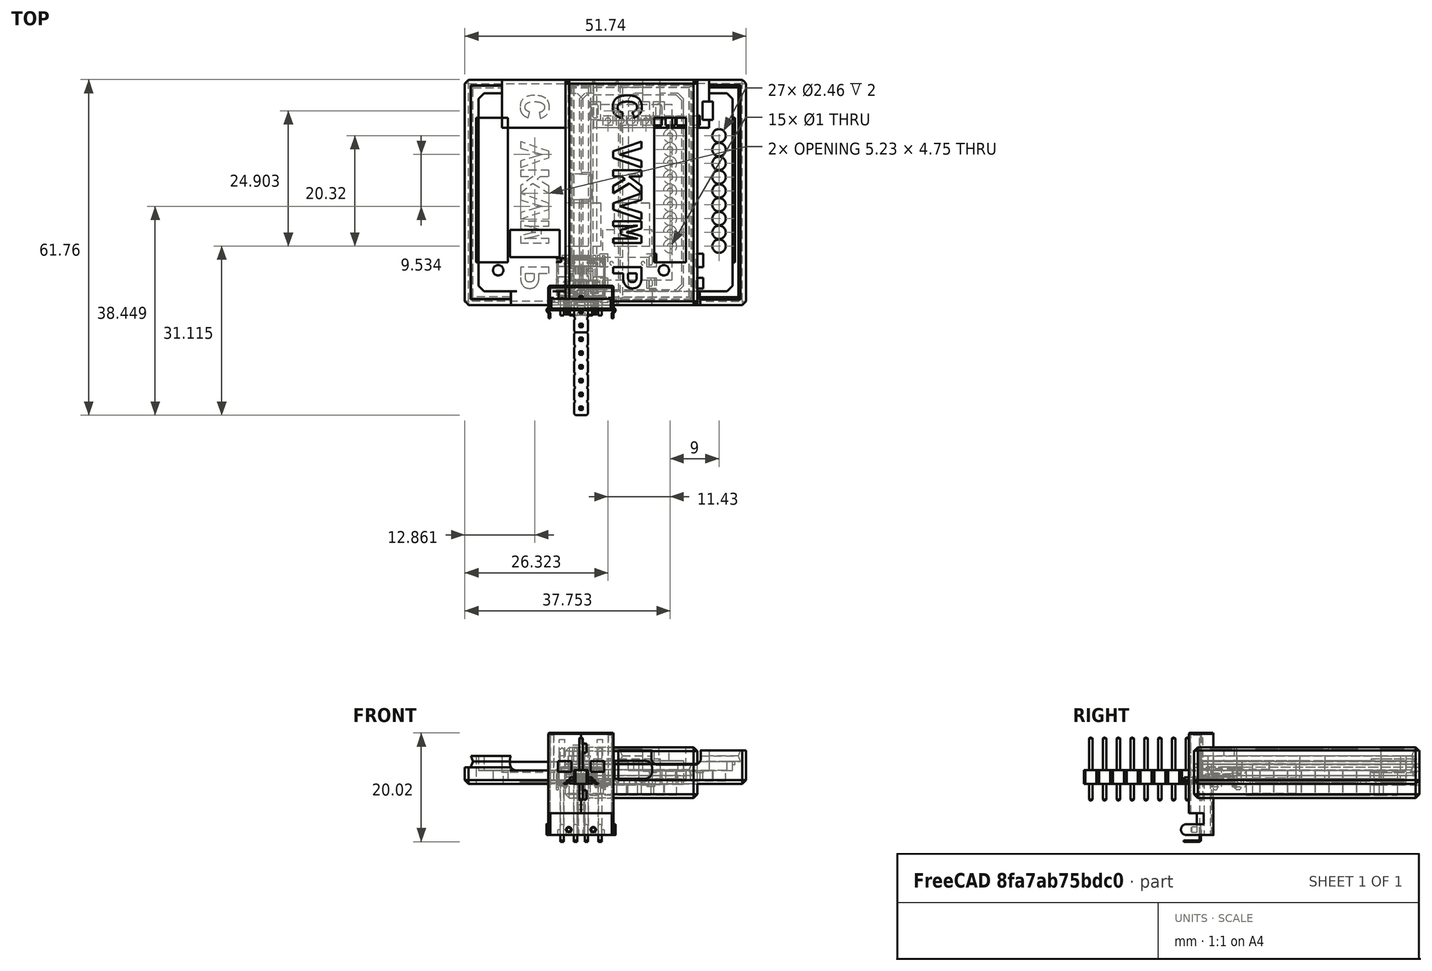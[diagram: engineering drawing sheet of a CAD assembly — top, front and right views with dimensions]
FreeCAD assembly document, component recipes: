
FREECAD ASSEMBLY — COMPONENT RECIPES ("case")

This assembly document has 10 components, labeled P0..P9 below (a component is one placed body or linked part). 4 of them carry a construction recipe — the FreeCAD feature program that regenerates the part from scratch, quoted from this document or its linked companion documents; the rest are supplied as boundary geometry only. No exploded tour is included for this assembly.
COMPONENT P0 — recipe-attached ("CaseAllPinsClone", modeled in this document).
Construction recipe (the document's own serialized feature program — sketch geometry with constraints, then the solid features built on it; lengths are millimeters unless a unit is written):

FEATURE [Sketcher::SketchObject] Sketch  label="OuterSketch"
  AttachmentOffset = pos=(0,0,-2.56) rot=(0,0,1;0rad)
  FullyConstrained = true
  MapMode = 5
  Placement = pos=(0,0,-2.56) rot=(0,0,1;0rad)
  Support = -> [XY_Plane031]
  expr: .AttachmentOffset.Base.z = -(<<Param>>.T_WALL + <<Param>>.T_Z)
  expr: .Constraints.X1 = -(<<Param>>.T_WALL + <<Param>>.S_SIDE + <<Param>>.T_XY)
  expr: .Constraints.X2 = 730 mil + <<Param>>.T_WALL + <<Param>>.S_SIDE + <<Param>>.T_XY
  expr: .Constraints.Y1 = 60 mil - <<Param>>.T_WALL - <<Param>>.S_SIDE - <<Param>>.T_XY
  expr: .Constraints.Y2 = 1470 mil + <<Param>>.T_WALL + <<Param>>.S_SIDE + <<Param>>.T_XY
  sketch-geometry (4):
    g0: LineSegment StartX=-2.83 StartY=-1.306 StartZ=0 EndX=21.372 EndY=-1.306 EndZ=0
    g1: LineSegment StartX=21.372 StartY=-1.306 StartZ=0 EndX=21.372 EndY=40.168 EndZ=0
    g2: LineSegment StartX=21.372 StartY=40.168 StartZ=0 EndX=-2.83 EndY=40.168 EndZ=0
    g3: LineSegment StartX=-2.83 StartY=40.168 StartZ=0 EndX=-2.83 EndY=-1.306 EndZ=0
  constraints (12):
    c: Coincident(g0,g1)
    c: Coincident(g1,g2)
    c: Coincident(g2,g3)
    c: Coincident(g3,g0)
    c: Horizontal(g0)
    c: Horizontal(g2)
    c: Vertical(g1)
    c: Vertical(g3)
    c: DistanceX(g0) = -2.83  'X1'
    c: DistanceY(g0) = -1.306  'Y1'
    c: DistanceX(g1) = 21.372  'X2'
    c: DistanceY(g1) = 40.168  'Y2'
FEATURE [PartDesign::Pad] Pad  label="OuterPad"
  Direction = (0,0,1)
  Length = 9.33
  Length2 = 10
  Profile = -> Sketch
  ReferenceAxis = -> Sketch [N_Axis]
  Type = 0
  expr: Length = <<Param>>.T_BOARD + 3.21 mm + 2 * (<<Param>>.T_WALL + <<Param>>.T_Z)
FEATURE [Sketcher::SketchObject] Sketch001  label="BoardSketch"
  AttachmentOffset = pos=(0,0,-0.06) rot=(0,0,1;0rad)
  FullyConstrained = true
  MapMode = 5
  Placement = pos=(0,0,-0.06) rot=(0,0,1;0rad)
  Support = -> [XY_Plane031]
  expr: .AttachmentOffset.Base.z = -<<Param>>.T_Z
  expr: Constraints[22] = <<OuterSketch>>.Constraints.Y1 + <<Param>>.T_WALL
  expr: Constraints[23] = <<OuterSketch>>.Constraints.X1 + <<Param>>.T_WALL
  expr: Constraints[24] = <<OuterSketch>>.Constraints.X2 - <<Param>>.T_WALL
  expr: Constraints[25] = <<OuterSketch>>.Constraints.Y2 - <<Param>>.T_WALL
  expr: Constraints[35] = max(0 mm; 0.76 mm - <<Param>>.S_SIDE - <<Param>>.T_XY)
  expr: Constraints[36] = 50 mil + <<Param>>.S_SIDE + <<Param>>.T_XY - min(0 mm; 0.76 mm - <<Param>>.S_SIDE - <<Param>>.T_XY)
  expr: Constraints[37] = 560 mil + 2 * (<<Param>>.S_SIDE + <<Param>>.T_XY)
  expr: Constraints[38] = 210 mil - 2 * (<<Param>>.S_SIDE + <<Param>>.T_XY)
  expr: Constraints[39] = 40 mil
  sketch-geometry (14):
    g0: LineSegment StartX=-0.33 StartY=2.21 StartZ=0 EndX=0.686 EndY=1.194 EndZ=0
    g1: LineSegment StartX=0.686 StartY=1.194 StartZ=0 EndX=17.856 EndY=1.194 EndZ=0
    g2: LineSegment StartX=17.856 StartY=1.194 StartZ=0 EndX=18.872 EndY=2.21 EndZ=0
    g3: LineSegment StartX=18.872 StartY=2.21 StartZ=0 EndX=18.872 EndY=36.652 EndZ=0
    g4: LineSegment StartX=18.872 StartY=36.652 StartZ=0 EndX=17.856 EndY=37.668 EndZ=0
    g5: LineSegment StartX=17.856 StartY=37.668 StartZ=0 EndX=0.686 EndY=37.668 EndZ=0
    g6: LineSegment StartX=0.686 StartY=37.668 StartZ=0 EndX=-0.33 EndY=36.652 EndZ=0
    g7: LineSegment StartX=-0.33 StartY=36.652 StartZ=0 EndX=-0.33 EndY=22.784 EndZ=0
    g8: LineSegment StartX=-0.33 StartY=22.784 StartZ=0 EndX=1.27 EndY=22.784 EndZ=0
    g9: LineSegment StartX=1.7 StartY=22.354 StartZ=0 EndX=1.7 EndY=18.54 EndZ=0
    g10: LineSegment StartX=1.27 StartY=18.11 StartZ=0 EndX=-0.33 EndY=18.11 EndZ=0
    g11: LineSegment StartX=-0.33 StartY=18.11 StartZ=0 EndX=-0.33 EndY=2.21 EndZ=0
    g12: ArcOfCircle CenterX=1.27 CenterY=22.354 CenterZ=0 NormalX=0 NormalY=0 NormalZ=1 AngleXU=0 Radius=0.43 StartAngle=-2.7e-15 EndAngle=1.5708
    g13: ArcOfCircle CenterX=1.27 CenterY=18.54 CenterZ=0 NormalX=0 NormalY=0 NormalZ=1 AngleXU=0 Radius=0.43 StartAngle=4.71239 EndAngle=6.28319
  constraints (40):
    c: Coincident(g0,g1)
    c: Horizontal(g1)
    c: Coincident(g1,g2)
    c: Coincident(g2,g3)
    c: Vertical(g3)
    c: Coincident(g3,g4)
    c: Coincident(g4,g5)
    c: Horizontal(g5)
    c: Coincident(g5,g6)
    c: Coincident(g6,g7)
    c: Vertical(g7)
    c: Coincident(g7,g8)
    c: Vertical(g9)
    c: Horizontal(g10)
    c: Coincident(g10,g11)
    c: Coincident(g11,g0)
    c: Vertical(g11)
    c: Horizontal(g0,g2)
    c: Vertical(g10,g7)
    c: Horizontal(g6,g3)
    c: Vertical(g5,g0)
    c: Vertical(g1,g4)
    c: DistanceY(g0) = 1.194
    c: DistanceX(g0) = -0.33
    c: DistanceX(g3) = 18.872
    c: DistanceY(g4) = 37.668
    c: Equal(g6,g4)
    c: Equal(g4,g2)
    c: Angle(g4,g3) = 2.35619
    c: Horizontal(g8)
    c: Tangent(g8,g12) = 1.5708
    c: Tangent(g9,g12) = 1.5708
    c: Tangent(g9,g13) = 1.5708
    c: Tangent(g10,g13) = 1.5708
    c: Equal(g13,g12)
    c: Radius(g12) = 0.43
    c: DistanceX(g8,g8) = 1.6
    c: DistanceY(g8,g5) = 14.884
    c: DistanceY(g10,g7) = 4.674
    c: DistanceX(g4,g4) = 1.016
FEATURE [Sketcher::SketchObject] Sketch002  label="LedSketch"
  FullyConstrained = true
  MapMode = 5
  Support = -> [XY_Plane031]
  expr: Constraints[0] = <<Param>>.D_LED + 2 * <<Param>>.T_XY
  expr: Constraints[1] = 600 mil
  expr: Constraints[2] = 200 mil
  sketch-geometry (1):
    g0: Circle CenterX=15.24 CenterY=5.08 CenterZ=0 NormalX=0 NormalY=0 NormalZ=1 AngleXU=0 Radius=0.955
  constraints (3):
    c: Diameter(g0) = 1.91
    c: DistanceX(g0) = 15.24
    c: DistanceY(g0) = 5.08
FEATURE [Sketcher::SketchObject] Sketch003  label="UsbCSketch"
  AttachmentOffset = pos=(0,0,-7.427) rot=(0,0,1;0rad)
  FullyConstrained = true
  MapMode = 5
  Placement = pos=(0,7.427,1.6e-15) rot=(1,0,0;1.5708rad)
  Support = -> [XZ_Plane031]
  expr: .AttachmentOffset.Base.z = -(5 mil + 7.3 mm)
  expr: .Constraints.D1 = 3.16 mm + 2 * <<Param>>.T_Z
  expr: .Constraints.R1 = 1.1 mm + <<Param>>.T_XY + <<Param>>.T_Z
  expr: .Constraints.W1 = 8.95 mm + 2 * <<Param>>.T_XY
  expr: .Constraints.X1 = 335 mil
  expr: .Constraints.Z1 = <<Param>>.T_BOARD + 0.05 mm - <<Param>>.T_Z
  sketch-geometry (9):
    g0: LineSegment StartX=5.194 StartY=4.27 StartZ=0 EndX=11.824 EndY=4.27 EndZ=0
    g1: LineSegment StartX=13.064 StartY=3.03 StartZ=0 EndX=13.064 EndY=2.23 EndZ=0
    g2: LineSegment StartX=11.824 StartY=0.99 StartZ=0 EndX=5.194 EndY=0.99 EndZ=0
    g3: LineSegment StartX=3.954 StartY=2.23 StartZ=0 EndX=3.954 EndY=3.03 EndZ=0
    g4: ArcOfCircle CenterX=5.194 CenterY=3.03 CenterZ=0 NormalX=0 NormalY=0 NormalZ=1 AngleXU=0 Radius=1.24 StartAngle=1.5708 EndAngle=3.14159
    g5: ArcOfCircle CenterX=5.194 CenterY=2.23 CenterZ=0 NormalX=0 NormalY=0 NormalZ=1 AngleXU=0 Radius=1.24 StartAngle=3.14159 EndAngle=4.71239
    g6: ArcOfCircle CenterX=11.824 CenterY=2.23 CenterZ=0 NormalX=0 NormalY=0 NormalZ=1 AngleXU=0 Radius=1.24 StartAngle=4.71239 EndAngle=6.28319
    g7: ArcOfCircle CenterX=11.824 CenterY=3.03 CenterZ=0 NormalX=0 NormalY=0 NormalZ=1 AngleXU=0 Radius=1.24 StartAngle=0 EndAngle=1.5708
    g8: GeomPoint X=8.509 Y=0.99 Z=0
  constraints (21):
    c: Horizontal(g0)
    c: Horizontal(g2)
    c: Vertical(g1)
    c: Vertical(g3)
    c: Tangent(g0,g4) = 1.5708
    c: Tangent(g3,g4) = 1.5708
    c: Tangent(g3,g5) = 1.5708
    c: Tangent(g2,g5) = 1.5708
    c: Tangent(g2,g6) = 1.5708
    c: Tangent(g1,g6) = 1.5708
    c: Tangent(g1,g7) = 1.5708
    c: Tangent(g0,g7) = 1.5708
    c: Equal(g7,g4)
    c: Equal(g4,g5)
    c: Equal(g5,g6)
    c: DistanceX(g3,g1) = 9.11  'W1'
    c: DistanceY(g2,g0) = 3.28  'D1'
    c: Symmetric(g2,g2,g8)
    c: Radius(g4) = 1.24  'R1'
    c: DistanceX(g8) = 8.509  'X1'
    c: DistanceY(g8) = 0.99  'Z1'
FEATURE [Sketcher::SketchObject] Sketch004  label="UsbCHoldSketch"
  AttachmentOffset = pos=(0,0,2.69) rot=(0,0,1;0rad)
  FullyConstrained = true
  MapMode = 5
  Placement = pos=(0,0,2.69) rot=(0,0,1;0rad)
  Support = -> [XY_Plane031]
  expr: .AttachmentOffset.Base.z = <<UsbCSketch>>.Constraints.Z1 + <<Param>>.T_Z + <<UsbCSketch>>.Constraints.D1 / 2
  expr: Constraints[10] = <<UsbCSketch>>.Constraints.X1
  expr: Constraints[11] = <<UsbCSketch>>.Placement.Base.y + <<Param>>.T_XY
  expr: Constraints[12] = <<UsbCSketch>>.Constraints.W1
  sketch-geometry (5):
    g0: LineSegment StartX=3.954 StartY=12.507 StartZ=0 EndX=13.064 EndY=12.507 EndZ=0
    g1: LineSegment StartX=13.064 StartY=12.507 StartZ=0 EndX=13.064 EndY=7.507 EndZ=0
    g2: LineSegment StartX=13.064 StartY=7.507 StartZ=0 EndX=3.954 EndY=7.507 EndZ=0
    g3: LineSegment StartX=3.954 StartY=7.507 StartZ=0 EndX=3.954 EndY=12.507 EndZ=0
    g4: GeomPoint X=8.509 Y=7.507 Z=0
  constraints (13):
    c: Coincident(g0,g1)
    c: Coincident(g1,g2)
    c: Coincident(g2,g3)
    c: Coincident(g3,g0)
    c: Horizontal(g0)
    c: Horizontal(g2)
    c: Vertical(g1)
    c: Vertical(g3)
    c: DistanceY(g1,g1) = 5
    c: Symmetric(g2,g1,g4)
    c: DistanceX(g4) = 8.509
    c: DistanceY(g4) = 7.507
    c: DistanceX(g0,g0) = 9.11
FEATURE [Sketcher::SketchObject] Sketch005  label="UsbATopSketch"
  AttachmentOffset = pos=(0,0,-31.33) rot=(0,0,1;0rad)
  FullyConstrained = true
  MapMode = 5
  Placement = pos=(0,31.33,7e-15) rot=(1,0,0;1.5708rad)
  Support = -> [XZ_Plane031]
  expr: .AttachmentOffset.Base.z = -31.33 mm
  expr: .Constraints.W1 = 12 mm + 2 * <<Param>>.T_XY
  expr: .Constraints.X1 = 8.453 mm
  expr: .Constraints.Z1 = <<Param>>.T_BOARD
  expr: .Constraints.Z2 = <<Param>>.T_BOARD + 3.6 mm + <<Param>>.T_Z
  sketch-geometry (5):
    g0: LineSegment StartX=2.373 StartY=4.66 StartZ=0 EndX=14.533 EndY=4.66 EndZ=0
    g1: LineSegment StartX=14.533 StartY=4.66 StartZ=0 EndX=14.533 EndY=1 EndZ=0
    g2: LineSegment StartX=14.533 StartY=1 StartZ=0 EndX=2.373 EndY=1 EndZ=0
    g3: LineSegment StartX=2.373 StartY=1 StartZ=0 EndX=2.373 EndY=4.66 EndZ=0
    g4: GeomPoint X=8.453 Y=1 Z=0
  constraints (13):
    c: Coincident(g0,g1)
    c: Coincident(g1,g2)
    c: Coincident(g2,g3)
    c: Coincident(g3,g0)
    c: Horizontal(g0)
    c: Horizontal(g2)
    c: Vertical(g1)
    c: Vertical(g3)
    c: DistanceY(g0) = 4.66  'Z2'
    c: Symmetric(g2,g1,g4)
    c: DistanceY(g1) = 1  'Z1'
    c: DistanceX(g2,g2) = 12.16  'W1'
    c: DistanceX(g4) = 8.453  'X1'
FEATURE [Sketcher::SketchObject] Sketch006  label="UsbABottomSketch"
  AttachmentOffset = pos=(0,0,-31.33) rot=(0,0,1;0rad)
  FullyConstrained = true
  MapMode = 5
  Placement = pos=(0,31.33,7e-15) rot=(1,0,0;1.5708rad)
  Support = -> [XZ_Plane031]
  expr: .AttachmentOffset.Base.z = -31.33 mm
  expr: .Constraints.W1 = <<UsbATopSketch>>.Constraints.W1
  expr: .Constraints.X1 = <<UsbATopSketch>>.Constraints.X1
  expr: .Constraints.Z2 = <<UsbATopSketch>>.Constraints.Z2
  expr: Constraints[13] = 4.7 mm + 2 * <<Param>>.T_Z
  sketch-geometry (5):
    g0: LineSegment StartX=2.373 StartY=4.66 StartZ=0 EndX=14.533 EndY=4.66 EndZ=0
    g1: LineSegment StartX=14.533 StartY=4.66 StartZ=0 EndX=14.533 EndY=-0.16 EndZ=0
    g2: LineSegment StartX=14.533 StartY=-0.16 StartZ=0 EndX=2.373 EndY=-0.16 EndZ=0
    g3: LineSegment StartX=2.373 StartY=-0.16 StartZ=0 EndX=2.373 EndY=4.66 EndZ=0
    g4: GeomPoint X=8.453 Y=-0.16 Z=0
  constraints (14):
    c: Coincident(g0,g1)
    c: Coincident(g1,g2)
    c: Coincident(g2,g3)
    c: Coincident(g3,g0)
    c: Horizontal(g0)
    c: Horizontal(g2)
    c: Vertical(g1)
    c: Vertical(g3)
    c: DistanceY(g0) = 4.66  'Z2'
    c: Symmetric(g2,g1,g4)
    c: DistanceY(g1) = -0.16  'Z1'
    c: DistanceX(g2,g2) = 12.16  'W1'
    c: DistanceX(g4) = 8.453  'X1'
    c: DistanceY(g1,g1) = 4.82
FEATURE [PartDesign::Chamfer] Chamfer  label="OuterChamfer"
  Angle = 45
  Base = -> Pad [Edge1,Edge2,Edge3,Edge4,Edge5,Edge6,Edge7,Edge8,Edge9,Edge10,Edge11,Edge12]
  BaseFeature = -> Pad
  ChamferType = 0
  FlipDirection = false
  Size = 0.7
  Size2 = 1
  SupportTransform = false
  UseAllEdges = true
  expr: Size = <<Param>>.R_CORNER
FEATURE [PartDesign::Pocket] Pocket  label="BoardPocket"
  BaseFeature = -> Chamfer
  Direction = (0,0,-1)
  Length = 4.33
  Length2 = 5
  Profile = -> Sketch001
  ReferenceAxis = -> Sketch001 [N_Axis]
  Reversed = true
  Type = 0
  expr: Length = <<Param>>.T_BOARD + 3.21 mm + 2 * <<Param>>.T_Z
FEATURE [PartDesign::Pocket] Pocket001  label="LedPocket"
  BaseFeature = -> Pocket
  Direction = (0,0,-1)
  Length = 5
  Length2 = 5
  Profile = -> Sketch002
  ReferenceAxis = -> Sketch002 [N_Axis]
  Reversed = true
  Type = 1
FEATURE [PartDesign::Pocket] Pocket002  label="UsbCPocket"
  BaseFeature = -> Pocket001
  Direction = (0,1,2e-16)
  Length = 5
  Length2 = 5
  Profile = -> Sketch003
  ReferenceAxis = -> Sketch003 [N_Axis]
  Reversed = true
  Type = 1
FEATURE [Sketcher::SketchObject] Sketch007  label="UsbCPinsSketch"
  FullyConstrained = true
  MapMode = 5
  Support = -> [XY_Plane031]
  expr: Constraints[89] = <<UsbCSketch>>.Constraints.X1
  expr: Constraints[90] = 5 mil + 6.25 mm
  expr: Constraints[91] = 5.78 mm
  expr: Constraints[92] = 0.65 mm + 2 * (<<Param>>.S_PIN + <<Param>>.T_XY)
  expr: Constraints[94] = 8.64 mm
  expr: Constraints[95] = 4.18 mm
  expr: Constraints[96] = 0.6 mm + 2 * (<<Param>>.S_PIN + <<Param>>.T_XY)
  expr: Constraints[97] = 1.7 mm + 2 * (<<Param>>.S_PIN + <<Param>>.T_XY)
  expr: Constraints[98] = 1.2 mm + 2 * (<<Param>>.S_PIN + <<Param>>.T_XY)
  sketch-geometry (38):
    g0: LineSegment StartX=3.509 StartY=8.137 StartZ=0 EndX=4.869 EndY=8.137 EndZ=0
    g1: LineSegment StartX=4.869 StartY=8.137 StartZ=0 EndX=4.869 EndY=5.677 EndZ=0
    g2: LineSegment StartX=4.869 StartY=5.677 StartZ=0 EndX=3.509 EndY=5.677 EndZ=0
    g3: LineSegment StartX=3.509 StartY=5.677 StartZ=0 EndX=3.509 EndY=8.137 EndZ=0
    g4: LineSegment StartX=3.509 StartY=3.707 StartZ=0 EndX=4.869 EndY=3.707 EndZ=0
    g5: LineSegment StartX=4.869 StartY=3.707 StartZ=0 EndX=4.869 EndY=1.747 EndZ=0
    g6: LineSegment StartX=4.869 StartY=1.747 StartZ=0 EndX=3.509 EndY=1.747 EndZ=0
    g7: LineSegment StartX=3.509 StartY=1.747 StartZ=0 EndX=3.509 EndY=3.707 EndZ=0
    g8: LineSegment StartX=12.149 StartY=3.707 StartZ=0 EndX=13.509 EndY=3.707 EndZ=0
    g9: LineSegment StartX=13.509 StartY=3.707 StartZ=0 EndX=13.509 EndY=1.747 EndZ=0
    g10: LineSegment StartX=13.509 StartY=1.747 StartZ=0 EndX=12.149 EndY=1.747 EndZ=0
    g11: LineSegment StartX=12.149 StartY=1.747 StartZ=0 EndX=12.149 EndY=3.707 EndZ=0
    g12: LineSegment StartX=12.149 StartY=8.137 StartZ=0 EndX=13.509 EndY=8.137 EndZ=0
    g13: LineSegment StartX=13.509 StartY=8.137 StartZ=0 EndX=13.509 EndY=5.677 EndZ=0
    g14: LineSegment StartX=13.509 StartY=5.677 StartZ=0 EndX=12.149 EndY=5.677 EndZ=0
    g15: LineSegment StartX=12.149 StartY=5.677 StartZ=0 EndX=12.149 EndY=8.137 EndZ=0
    g16: LineSegment StartX=10.694 StartY=7.082 StartZ=0 EndX=12.104 EndY=7.082 EndZ=0
    g17: LineSegment StartX=12.104 StartY=7.082 StartZ=0 EndX=12.104 EndY=5.672 EndZ=0
    g18: LineSegment StartX=12.104 StartY=5.672 StartZ=0 EndX=10.694 EndY=5.672 EndZ=0
    g19: LineSegment StartX=10.694 StartY=5.672 StartZ=0 EndX=10.694 EndY=7.082 EndZ=0
    g20: LineSegment StartX=4.914 StartY=7.082 StartZ=0 EndX=6.324 EndY=7.082 EndZ=0
    g21: LineSegment StartX=6.324 StartY=7.082 StartZ=0 EndX=6.324 EndY=5.672 EndZ=0
    g22: LineSegment StartX=6.324 StartY=5.672 StartZ=0 EndX=4.914 EndY=5.672 EndZ=0
    g23: LineSegment StartX=4.914 StartY=5.672 StartZ=0 EndX=4.914 EndY=7.082 EndZ=0
    g24: LineSegment StartX=4.189 StartY=2.727 StartZ=0 EndX=12.829 EndY=2.727 EndZ=0
    g25: LineSegment StartX=12.829 StartY=2.727 StartZ=0 EndX=12.829 EndY=6.907 EndZ=0
    g26: LineSegment StartX=12.829 StartY=6.907 StartZ=0 EndX=4.189 EndY=6.907 EndZ=0
    g27: LineSegment StartX=4.189 StartY=6.907 StartZ=0 EndX=4.189 EndY=2.727 EndZ=0
    g28: LineSegment StartX=5.619 StartY=6.377 StartZ=0 EndX=11.399 EndY=6.377 EndZ=0
    g29: LineSegment StartX=8.509 StartY=6.907 StartZ=0 EndX=8.509 EndY=6.377 EndZ=0
    g30: LineSegment StartX=4.869 StartY=8.137 StartZ=0 EndX=12.149 EndY=8.137 EndZ=0
    g31: LineSegment StartX=13.509 StartY=5.677 StartZ=0 EndX=13.509 EndY=3.707 EndZ=0
    g32: LineSegment StartX=12.149 StartY=1.747 StartZ=0 EndX=4.869 EndY=1.747 EndZ=0
    g33: LineSegment StartX=3.509 StartY=3.707 StartZ=0 EndX=3.509 EndY=5.677 EndZ=0
    g34: LineSegment StartX=4.869 StartY=5.677 StartZ=0 EndX=12.149 EndY=5.677 EndZ=0
    g35: LineSegment StartX=12.149 StartY=5.677 StartZ=0 EndX=12.149 EndY=3.707 EndZ=0
    g36: LineSegment StartX=12.149 StartY=3.707 StartZ=0 EndX=4.869 EndY=3.707 EndZ=0
    g37: LineSegment StartX=4.869 StartY=5.677 StartZ=0 EndX=4.869 EndY=3.707 EndZ=0
  constraints (100):
    c: Coincident(g0,g1)
    c: Coincident(g1,g2)
    c: Coincident(g2,g3)
    c: Coincident(g3,g0)
    c: Horizontal(g0)
    c: Horizontal(g2)
    c: Vertical(g1)
    c: Vertical(g3)
    c: Coincident(g4,g5)
    c: Coincident(g5,g6)
    c: Coincident(g6,g7)
    c: Coincident(g7,g4)
    c: Horizontal(g4)
    c: Horizontal(g6)
    c: Vertical(g5)
    c: Vertical(g7)
    c: Coincident(g8,g9)
    c: Coincident(g9,g10)
    c: Coincident(g10,g11)
    c: Coincident(g11,g8)
    c: Horizontal(g8)
    c: Horizontal(g10)
    c: Vertical(g9)
    c: Vertical(g11)
    c: Coincident(g12,g13)
    c: Coincident(g13,g14)
    c: Coincident(g14,g15)
    c: Coincident(g15,g12)
    c: Horizontal(g12)
    c: Horizontal(g14)
    c: Vertical(g13)
    c: Vertical(g15)
    c: Coincident(g16,g17)
    c: Coincident(g17,g18)
    c: Coincident(g18,g19)
    c: Coincident(g19,g16)
    c: Horizontal(g16)
    c: Horizontal(g18)
    c: Vertical(g17)
    c: Vertical(g19)
    c: Coincident(g20,g21)
    c: Coincident(g21,g22)
    c: Coincident(g22,g23)
    c: Coincident(g23,g20)
    c: Horizontal(g20)
    c: Horizontal(g22)
    c: Vertical(g21)
    c: Vertical(g23)
    c: Coincident(g24,g25)
    c: Coincident(g25,g26)
    c: Coincident(g26,g27)
    c: Coincident(g27,g24)
    c: Horizontal(g24)
    c: Horizontal(g26)
    c: Vertical(g25)
    c: Vertical(g27)
    c: Horizontal(g28)
    c: Symmetric(g16,g17,g28)
    c: Symmetric(g20,g21,g28)
    c: Symmetric(g0,g1,g26)
    c: Symmetric(g4,g5,g24)
    c: Symmetric(g8,g9,g24)
    c: Symmetric(g12,g13,g25)
    c: Vertical(g29)
    c: Symmetric(g25,g26,g29)
    c: Symmetric(g28,g28,g29)
    c: Equal(g20,g21)
    c: Equal(g16,g17)
    c: Coincident(g30,g0)
    c: Coincident(g30,g12)
    c: Horizontal(g30)
    c: Coincident(g31,g13)
    c: Coincident(g31,g8)
    c: Vertical(g31)
    c: Coincident(g32,g10)
    c: Coincident(g32,g5)
    c: Horizontal(g32)
    c: Coincident(g33,g4)
    c: Coincident(g33,g2)
    c: Vertical(g33)
    c: Coincident(g34,g1)
    c: Coincident(g34,g14)
    c: Coincident(g35,g14)
    c: Coincident(g35,g8)
    c: Coincident(g36,g8)
    c: Coincident(g36,g4)
    c: Coincident(g37,g1)
    c: Coincident(g37,g4)
    c: Equal(g8,g4)
    c: DistanceX(g29) = 8.509
    c: DistanceY(g29) = 6.377
    c: DistanceX(g28,g28) = 5.78
    c: DistanceX(g16,g16) = 1.41
    c: Equal(g20,g16)
    c: DistanceX(g26,g26) = 8.64
    c: DistanceY(g25,g25) = 4.18
    c: DistanceX(g12,g12) = 1.36
    c: DistanceY(g13,g13) = 2.46
    c: DistanceY(g9,g9) = 1.96
    c: DistanceY(g24,g28) = 3.65
FEATURE [PartDesign::Pocket] Pocket005  label="UsbCPinsPocket"
  BaseFeature = -> Pocket002
  Direction = (0,0,-1)
  Length = 0.5
  Length2 = 5
  Profile = -> Sketch007
  ReferenceAxis = -> Sketch007 [N_Axis]
  Type = 0
FEATURE [PartDesign::Pad] Pad001  label="UsbCHoldPad"
  BaseFeature = -> Pocket005
  Direction = (0,0,1)
  Length = 10
  Length2 = 10
  Profile = -> Sketch004
  ReferenceAxis = -> Sketch004 [N_Axis]
  Type = 1
FEATURE [PartDesign::Pocket] Pocket003  label="UsbATopPocket"
  BaseFeature = -> Pad001
  Direction = (0,1,2e-16)
  Length = 5
  Length2 = 5
  Profile = -> Sketch005
  ReferenceAxis = -> Sketch005 [N_Axis]
  Type = 1
FEATURE [PartDesign::Pocket] Pocket004  label="UsbABottomPocket"
  BaseFeature = -> Pocket003
  Direction = (0,1,2e-16)
  Length = 5
  Length2 = 5
  Profile = -> Sketch006
  ReferenceAxis = -> Sketch006 [N_Axis]
  Type = 1
FEATURE [Sketcher::SketchObject] Sketch008  label="UsbAPinsSketch"
  FullyConstrained = true
  MapMode = 5
  Support = -> [XY_Plane031]
  expr: Constraints[117] = 1 mm + 2 * (<<Param>>.S_PIN + <<Param>>.T_XY)
  expr: Constraints[119] = 1.2 mm + 2 * (<<Param>>.S_PIN + <<Param>>.T_XY)
  expr: Constraints[120] = 2.6 mm + 2 * (<<Param>>.S_PIN + <<Param>>.T_XY)
  expr: Constraints[125] = <<UsbATopSketch>>.Constraints.X1
  expr: Constraints[126] = <<UsbATopSketch>>.Placement.Base.y + <<Param>>.T_XY + 1.217 mm
  sketch-geometry (51):
    g0: LineSegment StartX=1.623 StartY=36.107 StartZ=0 EndX=3.583 EndY=36.107 EndZ=0
    g1: LineSegment StartX=3.583 StartY=36.107 StartZ=0 EndX=3.583 EndY=32.747 EndZ=0
    g2: LineSegment StartX=3.583 StartY=32.747 StartZ=0 EndX=1.623 EndY=32.747 EndZ=0
    g3: LineSegment StartX=1.623 StartY=32.747 StartZ=0 EndX=1.623 EndY=36.107 EndZ=0
    g4: LineSegment StartX=13.323 StartY=36.107 StartZ=0 EndX=15.283 EndY=36.107 EndZ=0
    g5: LineSegment StartX=15.283 StartY=36.107 StartZ=0 EndX=15.283 EndY=32.747 EndZ=0
    g6: LineSegment StartX=15.283 StartY=32.747 StartZ=0 EndX=13.323 EndY=32.747 EndZ=0
    g7: LineSegment StartX=13.323 StartY=32.747 StartZ=0 EndX=13.323 EndY=36.107 EndZ=0
    g8: LineSegment StartX=5.328 StartY=35.307 StartZ=0 EndX=7.088 EndY=35.307 EndZ=0
    g9: LineSegment StartX=7.088 StartY=35.307 StartZ=0 EndX=7.088 EndY=33.547 EndZ=0
    g10: LineSegment StartX=7.088 StartY=33.547 StartZ=0 EndX=5.328 EndY=33.547 EndZ=0
    g11: LineSegment StartX=5.328 StartY=33.547 StartZ=0 EndX=5.328 EndY=35.307 EndZ=0
    g12: LineSegment StartX=9.818 StartY=35.307 StartZ=0 EndX=11.578 EndY=35.307 EndZ=0
    g13: LineSegment StartX=11.578 StartY=35.307 StartZ=0 EndX=11.578 EndY=33.547 EndZ=0
    g14: LineSegment StartX=11.578 StartY=33.547 StartZ=0 EndX=9.818 EndY=33.547 EndZ=0
    g15: LineSegment StartX=9.818 StartY=33.547 StartZ=0 EndX=9.818 EndY=35.307 EndZ=0
    g16: LineSegment StartX=4.073 StartY=33.507 StartZ=0 EndX=5.833 EndY=33.507 EndZ=0
    g17: LineSegment StartX=5.833 StartY=33.507 StartZ=0 EndX=5.833 EndY=31.747 EndZ=0
    g18: LineSegment StartX=5.833 StartY=31.747 StartZ=0 EndX=4.073 EndY=31.747 EndZ=0
    g19: LineSegment StartX=4.073 StartY=31.747 StartZ=0 EndX=4.073 EndY=33.507 EndZ=0
    g20: LineSegment StartX=6.573 StartY=33.507 StartZ=0 EndX=8.333 EndY=33.507 EndZ=0
    g21: LineSegment StartX=8.333 StartY=33.507 StartZ=0 EndX=8.333 EndY=31.747 EndZ=0
    g22: LineSegment StartX=8.333 StartY=31.747 StartZ=0 EndX=6.573 EndY=31.747 EndZ=0
    g23: LineSegment StartX=6.573 StartY=31.747 StartZ=0 EndX=6.573 EndY=33.507 EndZ=0
    g24: LineSegment StartX=8.573 StartY=33.507 StartZ=0 EndX=10.333 EndY=33.507 EndZ=0
    g25: LineSegment StartX=10.333 StartY=33.507 StartZ=0 EndX=10.333 EndY=31.747 EndZ=0
    g26: LineSegment StartX=10.333 StartY=31.747 StartZ=0 EndX=8.573 EndY=31.747 EndZ=0
    g27: LineSegment StartX=8.573 StartY=31.747 StartZ=0 EndX=8.573 EndY=33.507 EndZ=0
    g28: LineSegment StartX=11.073 StartY=33.507 StartZ=0 EndX=12.833 EndY=33.507 EndZ=0
    g29: LineSegment StartX=12.833 StartY=33.507 StartZ=0 EndX=12.833 EndY=31.747 EndZ=0
    g30: LineSegment StartX=12.833 StartY=31.747 StartZ=0 EndX=11.073 EndY=31.747 EndZ=0
    g31: LineSegment StartX=11.073 StartY=31.747 StartZ=0 EndX=11.073 EndY=33.507 EndZ=0
    g32: LineSegment StartX=2.603 StartY=34.427 StartZ=0 EndX=14.303 EndY=34.427 EndZ=0
    g33: LineSegment StartX=14.303 StartY=34.427 StartZ=0 EndX=14.303 EndY=32.627 EndZ=0
    g34: LineSegment StartX=14.303 StartY=32.627 StartZ=0 EndX=2.603 EndY=32.627 EndZ=0
    g35: LineSegment StartX=2.603 StartY=32.627 StartZ=0 EndX=2.603 EndY=34.427 EndZ=0
    g36: GeomPoint X=4.953 Y=32.627 Z=0
    g37: GeomPoint X=7.453 Y=32.627 Z=0
    g38: GeomPoint X=9.453 Y=32.627 Z=0
    g39: GeomPoint X=11.953 Y=32.627 Z=0
    g40: LineSegment StartX=3.583 StartY=36.107 StartZ=0 EndX=13.323 EndY=36.107 EndZ=0
    g41: LineSegment StartX=13.323 StartY=32.747 StartZ=0 EndX=3.583 EndY=32.747 EndZ=0
    g42: LineSegment StartX=7.088 StartY=35.307 StartZ=0 EndX=9.818 EndY=35.307 EndZ=0
    g43: LineSegment StartX=7.088 StartY=33.547 StartZ=0 EndX=9.818 EndY=33.547 EndZ=0
    g44: LineSegment StartX=5.833 StartY=33.507 StartZ=0 EndX=6.573 EndY=33.507 EndZ=0
    g45: LineSegment StartX=8.333 StartY=33.507 StartZ=0 EndX=8.573 EndY=33.507 EndZ=0
    g46: LineSegment StartX=10.333 StartY=33.507 StartZ=0 EndX=11.073 EndY=33.507 EndZ=0
    g47: GeomPoint X=6.208 Y=34.427 Z=0
    g48: GeomPoint X=10.698 Y=34.427 Z=0
    g49: GeomPoint X=8.453 Y=32.627 Z=0
    g50: GeomPoint X=8.453 Y=34.427 Z=0
  constraints (127):
    c: Coincident(g0,g1)
    c: Coincident(g1,g2)
    c: Coincident(g2,g3)
    c: Coincident(g3,g0)
    c: Horizontal(g0)
    c: Horizontal(g2)
    c: Vertical(g1)
    c: Vertical(g3)
    c: Coincident(g4,g5)
    c: Coincident(g5,g6)
    c: Coincident(g6,g7)
    c: Coincident(g7,g4)
    c: Horizontal(g4)
    c: Horizontal(g6)
    c: Vertical(g5)
    c: Vertical(g7)
    c: Coincident(g8,g9)
    c: Coincident(g9,g10)
    c: Coincident(g10,g11)
    c: Coincident(g11,g8)
    c: Horizontal(g8)
    c: Horizontal(g10)
    c: Vertical(g9)
    c: Vertical(g11)
    c: Coincident(g12,g13)
    c: Coincident(g13,g14)
    c: Coincident(g14,g15)
    c: Coincident(g15,g12)
    c: Horizontal(g12)
    c: Horizontal(g14)
    c: Vertical(g13)
    c: Vertical(g15)
    c: Coincident(g16,g17)
    c: Coincident(g17,g18)
    c: Coincident(g18,g19)
    c: Coincident(g19,g16)
    c: Horizontal(g16)
    c: Horizontal(g18)
    c: Vertical(g17)
    c: Vertical(g19)
    c: Coincident(g20,g21)
    c: Coincident(g21,g22)
    c: Coincident(g22,g23)
    c: Coincident(g23,g20)
    c: Horizontal(g20)
    c: Horizontal(g22)
    c: Vertical(g21)
    c: Vertical(g23)
    c: Coincident(g24,g25)
    c: Coincident(g25,g26)
    c: Coincident(g26,g27)
    c: Coincident(g27,g24)
    c: Horizontal(g24)
    c: Horizontal(g26)
    c: Vertical(g25)
    c: Vertical(g27)
    c: Coincident(g28,g29)
    c: Coincident(g29,g30)
    c: Coincident(g30,g31)
    c: Coincident(g31,g28)
    c: Horizontal(g28)
    c: Horizontal(g30)
    c: Vertical(g29)
    c: Vertical(g31)
    c: Coincident(g32,g33)
    c: Coincident(g33,g34)
    c: Coincident(g34,g35)
    c: Coincident(g35,g32)
    c: Horizontal(g32)
    c: Horizontal(g34)
    c: Vertical(g33)
    c: Vertical(g35)
    c: PointOnObject(g36,g34)
    c: PointOnObject(g37,g34)
    c: PointOnObject(g39,g34)
    c: Symmetric(g0,g1,g32)
    c: Symmetric(g4,g5,g32)
    c: Symmetric(g16,g17,g36)
    c: Symmetric(g20,g21,g37)
    c: Symmetric(g24,g25,g38)
    c: Symmetric(g28,g29,g39)
    c: Equal(g28,g29)
    c: Equal(g24,g25)
    c: Equal(g20,g21)
    c: Equal(g16,g17)
    c: Equal(g8,g9)
    c: Equal(g12,g13)
    c: Coincident(g40,g0)
    c: Coincident(g40,g4)
    c: Horizontal(g40)
    c: Coincident(g41,g6)
    c: Coincident(g41,g1)
    c: Equal(g0,g4)
    c: Coincident(g42,g8)
    c: Coincident(g42,g12)
    c: Horizontal(g42)
    c: Coincident(g43,g9)
    c: Coincident(g43,g14)
    c: Horizontal(g43)
    c: Coincident(g44,g16)
    c: Coincident(g44,g20)
    c: Horizontal(g44)
    c: Coincident(g45,g20)
    c: Coincident(g45,g24)
    c: Horizontal(g45)
    c: Coincident(g46,g24)
    c: Coincident(g46,g28)
    c: Horizontal(g46)
    c: Equal(g44,g46)
    c: DistanceX(g36,g39) = 7
    c: DistanceX(g37,g38) = 2
    c: DistanceX(g32,g32) = 11.7
    c: DistanceY(g36,g32) = 1.8
    c: PointOnObject(g47,g32)
    c: Symmetric(g12,g13,g48)
    c: Symmetric(g8,g9,g47)
    c: DistanceX(g47,g48) = 4.49
    c: DistanceX(g8,g8) = 1.76
    c: Equal(g8,g16)
    c: DistanceX(g0,g0) = 1.96
    c: DistanceY(g3,g3) = 3.36
    c: Symmetric(g34,g33,g49)
    c: Symmetric(g37,g38,g49)
    c: Symmetric(g48,g47,g50)
    c: Vertical(g49,g50)
    c: DistanceX(g49) = 8.453
    c: DistanceY(g49) = 32.627
FEATURE [PartDesign::Pocket] Pocket006  label="UsbAPinsPocket"
  BaseFeature = -> Pocket004
  Direction = (0,0,-1)
  Length = 2.06
  Length2 = 5
  Profile = -> Sketch008
  ReferenceAxis = -> Sketch008 [N_Axis]
  Type = 0
  expr: Length = 2 mm + <<Param>>.T_Z
FEATURE [Sketcher::SketchObject] Sketch009  label="DebugPinsTopSketch"
  AttachmentOffset = pos=(0,0,1) rot=(0,0,1;0rad)
  FullyConstrained = true
  MapMode = 5
  Placement = pos=(0,0,1) rot=(0,0,1;0rad)
  Support = -> [XY_Plane031]
  expr: .AttachmentOffset.Base.z = <<Param>>.T_BOARD
  expr: .Constraints.H1 = 50 mil + <<Param>>.T_CONN_WALL + <<Param>>.T_XY
  expr: .Constraints.X1 = 645 mil
  expr: .Constraints.Y1 = 375 mil
  expr: Constraints[14] = .Constraints.H1 * 9
  sketch-geometry (6):
    g0: LineSegment StartX=13.433 StartY=33.125 StartZ=0 EndX=19.333 EndY=33.125 EndZ=0
    g1: LineSegment StartX=19.333 StartY=33.125 StartZ=0 EndX=19.333 EndY=6.575 EndZ=0
    g2: LineSegment StartX=13.433 StartY=6.575 StartZ=0 EndX=13.433 EndY=33.125 EndZ=0
    g3: LineSegment StartX=16.383 StartY=6.575 StartZ=0 EndX=16.383 EndY=9.525 EndZ=0
    g4: LineSegment StartX=19.333 StartY=6.575 StartZ=0 EndX=16.383 EndY=6.575 EndZ=0
    g5: LineSegment StartX=16.383 StartY=6.575 StartZ=0 EndX=13.433 EndY=6.575 EndZ=0
  constraints (17):
    c: Coincident(g0,g1)
    c: Coincident(g1,g4)
    c: Coincident(g5,g2)
    c: Coincident(g2,g0)
    c: Horizontal(g0)
    c: Vertical(g1)
    c: Vertical(g2)
    c: Vertical(g3)
    c: Symmetric(g1,g5,g3)
    c: DistanceY(g3,g3) = 2.95  'H1'
    c: Coincident(g4,g5)
    c: Horizontal(g4)
    c: Coincident(g3,g4)
    c: Equal(g3,g4)
    c: DistanceY(g1,g1) = 26.55
    c: DistanceX(g3) = 16.383  'X1'
    c: DistanceY(g3) = 9.525  'Y1'
FEATURE [PartDesign::Pocket] Pocket007  label="DebugPinsTopPocket"
  BaseFeature = -> Pocket006
  Direction = (0,0,-1)
  Length = 5
  Length2 = 5
  Profile = -> Sketch009
  ReferenceAxis = -> Sketch009 [N_Axis]
  Reversed = true
  Type = 1
FEATURE [Sketcher::SketchObject] Sketch010  label="DebugPinsBottomSketch"
  AttachmentOffset = pos=(0,0,-2.06) rot=(0,0,1;0rad)
  FullyConstrained = true
  MapMode = 5
  Placement = pos=(0,0,-2.06) rot=(0,0,1;0rad)
  Support = -> [XY_Plane031]
  expr: .AttachmentOffset.Base.z = -(2 mm + <<Param>>.T_Z)
  expr: Constraints[0] = <<DebugPinsTopSketch>>.Constraints.X1
  expr: Constraints[1] = <<DebugPinsTopSketch>>.Constraints.Y1
  expr: Constraints[2] = 0.85 mm + <<Param>>.S_PIN + <<Param>>.T_XY
  sketch-geometry (1):
    g0: Circle CenterX=16.383 CenterY=9.525 CenterZ=0 NormalX=0 NormalY=0 NormalZ=1 AngleXU=0 Radius=1.23
  constraints (3):
    c: DistanceX(g0) = 16.383
    c: DistanceY(g0) = 9.525
    c: Radius(g0) = 1.23
FEATURE [PartDesign::Pocket] Pocket008  label="DebugPinsBottomPocket"
  BaseFeature = -> Pocket007
  Direction = (0,0,-1)
  Length = 5
  Length2 = 5
  Profile = -> Sketch010
  ReferenceAxis = -> Sketch010 [N_Axis]
  Reversed = true
  Type = 1
FEATURE [PartDesign::LinearPattern] LinearPattern  label="DebugPinsBottomPattern"
  BaseFeature = -> Pocket008
  Direction = -> Y_Axis031
  Length = 20.32
  Occurrences = 9
  Originals = -> [Pocket008]
  expr: Length = 800 mil
FEATURE [Sketcher::SketchObject] Sketch011  label="SerialPinsSketch"
  AttachmentOffset = pos=(0,0,3.636) rot=(0,0,1;0rad)
  FullyConstrained = true
  MapMode = 5
  Placement = pos=(3.636,-8e-16,8e-16) rot=(0.57735,0.57735,0.57735;2.0944rad)
  Support = -> [YZ_Plane031]
  expr: .AttachmentOffset.Base.z = 140 mil + <<Param>>.T_XY
  expr: .Constraints.D1 = 100 mil + 2 * <<Param>>.T_Z + 0.3 mm
  expr: .Constraints.H1 = 300 mil + 2 * <<Param>>.T_XY + 0.2 mm
  expr: .Constraints.Y1 = 430 mil
  expr: .Constraints.Z1 = -(0.34 mm / 2 + 0.13 mm)
  expr: Constraints[12] = (.Constraints.H1 - 300 mil) / 2 + 50 mil
  sketch-geometry (5):
    g0: LineSegment StartX=9.472 StartY=1.18 StartZ=0 EndX=17.452 EndY=1.18 EndZ=0
    g1: LineSegment StartX=17.452 StartY=1.18 StartZ=0 EndX=17.452 EndY=-1.78 EndZ=0
    g2: LineSegment StartX=17.452 StartY=-1.78 StartZ=0 EndX=9.472 EndY=-1.78 EndZ=0
    g3: LineSegment StartX=9.472 StartY=-1.78 StartZ=0 EndX=9.472 EndY=1.18 EndZ=0
    g4: LineSegment StartX=9.472 StartY=-0.3 StartZ=0 EndX=10.922 EndY=-0.3 EndZ=0
  constraints (15):
    c: Coincident(g0,g1)
    c: Coincident(g1,g2)
    c: Coincident(g2,g3)
    c: Coincident(g3,g0)
    c: Horizontal(g0)
    c: Horizontal(g2)
    c: Vertical(g1)
    c: Vertical(g3)
    c: DistanceX(g2,g2) = 7.98  'H1'
    c: DistanceY(g1,g1) = 2.96  'D1'
    c: Horizontal(g4)
    c: Symmetric(g0,g2,g4)
    c: DistanceX(g4,g4) = 1.45
    c: DistanceX(g4) = 10.922  'Y1'
    c: DistanceY(g4) = -0.3  'Z1'
FEATURE [PartDesign::Pocket] Pocket009  label="SerialPinsPocket"
  BaseFeature = -> LinearPattern
  Direction = (-1,2e-16,-3e-16)
  Length = 5
  Length2 = 5
  Profile = -> Sketch011
  ReferenceAxis = -> Sketch011 [N_Axis]
  Type = 1
FEATURE [PartDesign::Body] Body  label="Case"
  Group = -> [Sketch,Pad,Sketch001,Chamfer,Pocket,Sketch002,Pocket001,Sketch003,Pocket002,Pocket005,Sketch004,Pad001,Sketch005,Pocket003,Sketch006,Pocket004,Sketch007,Sketch008,Pocket006,Sketch009,Pocket007,Sketch010,Pocket008,LinearPattern,Sketch011,Pocket009]
  Origin = -> Origin031
  Tip = -> Pocket009
COMPONENT P1 — recipe-attached ("GapAllPinsClone", modeled in this document).
Construction recipe (the document's own serialized feature program — sketch geometry with constraints, then the solid features built on it; lengths are millimeters unless a unit is written):

FEATURE [Sketcher::SketchObject] Sketch012  label="GapProfileSketch"
  AttachmentOffset = pos=(0,0,-2.306) rot=(0,0,1;0rad)
  FullyConstrained = true
  MapMode = 5
  Placement = pos=(0,2.306,5e-16) rot=(1,0,0;1.5708rad)
  Support = -> [XZ_Plane062]
  expr: .AttachmentOffset.Base.z = <<OuterSketch>>.Constraints.Y1 - 1 mm
  expr: Constraints[29] = <<Param>>.T_Z
  expr: Constraints[30] = <<Param>>.T_XY
  expr: Constraints[31] = <<Param>>.H_LATCH
  expr: Constraints[32] = -(<<Param>>.S_SIDE + <<Param>>.T_XY)
  expr: Constraints[33] = <<OuterSketch>>.Constraints.X1
  expr: Constraints[36] = <<UsbCSketch>>.Constraints.Z1 + <<UsbCSketch>>.Constraints.D1 / 2
  expr: Constraints[38] = <<Param>>.W_LATCH
  sketch-geometry (13):
    g0: LineSegment StartX=-2.83 StartY=3.63 StartZ=0 EndX=-1.83 EndY=3.63 EndZ=0
    g1: LineSegment StartX=-1.83 StartY=3.63 StartZ=0 EndX=-1.41 EndY=2.63 EndZ=0
    g2: LineSegment StartX=-1.41 StartY=2.63 StartZ=0 EndX=-1.83 EndY=1.57 EndZ=0
    g3: LineSegment StartX=-1.83 StartY=1.57 StartZ=0 EndX=1.77 EndY=1.57 EndZ=0
    g4: LineSegment StartX=1.77 StartY=1.57 StartZ=0 EndX=1.77 EndY=1.63 EndZ=0
    g5: LineSegment StartX=1.77 StartY=1.63 StartZ=0 EndX=-1.72623 EndY=1.63 EndZ=0
    g6: LineSegment StartX=-1.72623 StartY=1.63 StartZ=0 EndX=-1.33 EndY=2.63 EndZ=0
    g7: LineSegment StartX=-1.33 StartY=2.63 StartZ=0 EndX=-1.7752 EndY=3.69 EndZ=0
    g8: LineSegment StartX=-1.7752 StartY=3.69 StartZ=0 EndX=-2.83 EndY=3.69 EndZ=0
    g9: LineSegment StartX=-2.83 StartY=3.69 StartZ=0 EndX=-2.83 EndY=3.63 EndZ=0
    g10: LineSegment StartX=-1.33 StartY=2.63 StartZ=0 EndX=-0.33 EndY=2.63 EndZ=0
    g11: LineSegment StartX=-0.33 StartY=2.63 StartZ=0 EndX=-0.33 EndY=1.63 EndZ=0
    g12: LineSegment StartX=-1.83 StartY=3.63 StartZ=0 EndX=-1.83 EndY=2.63 EndZ=0
  constraints (39):
    c: Horizontal(g0)
    c: Coincident(g0,g1)
    c: Coincident(g1,g2)
    c: Coincident(g2,g3)
    c: Horizontal(g3)
    c: Coincident(g3,g4)
    c: Vertical(g4)
    c: Coincident(g4,g5)
    c: Horizontal(g5)
    c: Coincident(g5,g6)
    c: Coincident(g6,g7)
    c: Coincident(g7,g8)
    c: Horizontal(g8)
    c: Coincident(g8,g9)
    c: Coincident(g9,g0)
    c: Vertical(g9)
    c: Vertical(g0,g2)
    c: Equal(g4,g9)
    c: Coincident(g10,g6)
    c: Horizontal(g10)
    c: Coincident(g11,g10)
    c: PointOnObject(g11,g5)
    c: Vertical(g11)
    c: Coincident(g12,g0)
    c: Vertical(g12)
    c: Equal(g12,g11)
    c: Horizontal(g1,g6)
    c: Parallel(g2,g6)
    c: Parallel(g1,g7)
    c: DistanceY(g4,g4) = 0.06
    c: DistanceX(g1,g6) = 0.08
    c: DistanceY(g5,g0) = 2
    c: DistanceX(g10) = -0.33
    c: DistanceX(g8) = -2.83
    c: DistanceX(g11,g4) = 2.1
    c: Horizontal(g12,g1)
    c: DistanceY(g12) = 2.63
    c: Equal(g0,g10)
    c: DistanceX(g0,g6) = 0.5
FEATURE [PartDesign::AdditivePipe] AdditivePipe
  AuxilleryCurvelinear = true
  AuxillerySpineTangent = false
  Binormal = (0,0,0)
  Mode = 0
  Placement = pos=(0,0,0) rot=(1,0,0;1.5708rad)
  Profile = -> Sketch012
  Spine = -> Sketch
  SpineTangent = false
  Transformation = 0
  Transition = 1
FEATURE [PartDesign::Body] Body001  label="Gap"
  Group = -> [Sketch012,AdditivePipe]
  Origin = -> Origin062
  Tip = -> AdditivePipe
COMPONENT P2 — geometry summary ("LabelsAllPinsClone"; no construction recipe available for this part):
  bounding box: 35.5 x 5.4 x 0.4 mm
  tessellated surface: 2,110 triangles
  volume: 28 mm^3 (37% of its bounding box)
  symmetry: mirror-symmetric across its z mid-plane
COMPONENT P3 — geometry summary ("CaseDebugPinsClone"; no construction recipe available for this part):
  bounding box: 41.5 x 24.2 x 9.3 mm
  tessellated surface: 6,196 triangles
  volume: 5549 mm^3 (59% of its bounding box)
COMPONENT P4 — geometry summary ("LabelsDebugPinsClone"; no construction recipe available for this part):
  bounding box: 35.5 x 5.4 x 0.4 mm
  tessellated surface: 2,110 triangles
  volume: 28 mm^3 (37% of its bounding box)
  symmetry: mirror-symmetric across its z mid-plane
COMPONENT P5 — same part as P1; its construction recipe is shown at P1.
COMPONENT P6 — geometry summary ("CaseBaseClone"; no construction recipe available for this part):
  bounding box: 41.5 x 24.2 x 9.3 mm
  tessellated surface: 1,624 triangles
  volume: 6065 mm^3 (65% of its bounding box)
COMPONENT P7 — geometry summary ("LabelsBaseClone"; no construction recipe available for this part):
  bounding box: 35.5 x 5.4 x 0.4 mm
  tessellated surface: 2,110 triangles
  volume: 28 mm^3 (37% of its bounding box)
  symmetry: mirror-symmetric across its z mid-plane
COMPONENT P8 — same part as P1; its construction recipe is shown at P1.
COMPONENT P9 — geometry summary ("vkm.kicad_pcb"; no construction recipe available for this part):
  bounding box: 52.1 x 27.2 x 11.5 mm
  tessellated surface: 86,126 triangles
  volume: 1757 mm^3 (11% of its bounding box)
PROVENANCE & LICENSES
A FreeCAD (.FCStd) document from a public repository crawl; recipes are the document's own serialized feature recipes (and, for linked parts, companion documents' recipes).
License: gpl-2.0.
